# Revit family: METEOR_Atria II 6_REVIT_File (Standard)
name_source: partatom
category: Lighting Fixtures
revit_build: Autodesk Revit 2017 (Build: 20160225_1515(x64)
units: mm (PartAtom-declared; Revit-internal decimal feet)

## family parameters
Always vertical = Yes
Cut with Voids When Loaded = No
Host = Ceiling
Light Source = Yes
OmniClass Number = 23.80.70.11
OmniClass Title = Luminaries for Internal Lighting
Part Type = Normal
Room Calculation Point = No
Round Connector Dimension = Use Diameter
Shared = No

## types (48) — shared parameters
Color Filter = 16777215
Dimming Lamp Color Temperature Shift = <None>
Tilt Angle = 90.00°

## per-type parameters (varying)
| type | Photometric Web File |
| ASII6-60W-278-40 | ASII6-60-278-XXX-XXX-40-XXX.ies |
| ASII6-60W-278-60 | ASII6-60-278-XXX-XXX-60-XXX.ies |
| ASII6-60W-278-WD | ASII6-60-278-XXX-XXX-WD-XXX-DF.ies |
| ASII6-60W-308-40 | ASII6-60-308-XXX-XXX-40-XXX.ies |
| ASII6-60W-308-60 | ASII6-60-308-XXX-XXX-60-XXX.ies |
| ASII6-60W-308-WD | ASII6-60-308-XXX-XXX-WD-XXX-DF.ies |
| ASII6-60W-358-40 | ASII6-60-358-XXX-XXX-40-XXX.ies |
| ASII6-60W-358-60 | ASII6-60-358-XXX-XXX-60-XXX.ies |
| ASII6-60W-358-WD | ASII6-60-358-XXX-XXX-WD-XXX-DF.ies |
| ASII6-60W-408-40 | ASII6-60-408-XXX-XXX-40-XXX.ies |
| ASII6-40W-278-40 | ASII6-40-278-XXX-XXX-40-XXX.ies |
| ASII6-40W-278-60 | ASII6-40-278-XXX-XXX-60-XXX.ies |
| ASII6-40W-278-WD | ASII6-40-278-XXX-XXX-WD-XXX-DF.ies |
| ASII6-60W-408-60 | ASII6-60-408-XXX-XXX-60-XXX.ies |
| ASII6-60W-408-WD | ASII6-60-408-XXX-XXX-WD-XXX-DF.ies |
| ASII6-40W-308-40 | ASII6-40-308-XXX-XXX-40-XXX.ies |
| ASII6-40W-308-60 | ASII6-40-308-XXX-XXX-60-XXX.ies |
| ASII6-40W-308-WD | ASII6-40-308-XXX-XXX-WD-XXX-DF.ies |
| ASII6-40W-358-40 | ASII6-40-358-XXX-XXX-40-XXX.ies |
| ASII6-40W-358-60 | ASII6-40-358-XXX-XXX-60-XXX.ies |
| ASII6-40W-358-WD | ASII6-40-358-XXX-XXX-WD-XXX-DF.ies |
| ASII6-40W-408-40 | ASII6-40-408-XXX-XXX-40-XXX.ies |
| ASII6-40W-408-60 | ASII6-40-408-XXX-XXX-60-XXX.ies |
| ASII6-40W-408-WD | ASII6-40-408-XXX-XXX-WD-XXX-DF.ies |
| ASII6-80W-278-40 | ASII6-80-278-XXX-XXX-40-XXX.ies |
| ASII6-80W-278-60 | ASII6-80-278-XXX-XXX-60-XXX.ies |
| ASII6-80W-278-WD | ASII6-80-278-XXX-XXX-WD-XXX-DF.ies |
| ASII6-80W-308-40 | ASII6-80-308-XXX-XXX-40-XXX.ies |
| ASII6-80W-308-60 | ASII6-80-308-XXX-XXX-60-XXX.ies |
| ASII6-80W-308-WD | ASII6-80-308-XXX-XXX-60-XXX.ies |
| ASII6-80W-358-40 | ASII6-80-358-XXX-XXX-40-XXX.ies |
| ASII6-80W-358-60 | ASII6-80-358-XXX-XXX-60-XXX.ies |
| ASII6-80W-358-WD | ASII6-80-358-XXX-XXX-WD-XXX-DF.ies |
| ASII6-80W-408-40 | ASII6-80-408-XXX-XXX-40-XXX.ies |
| ASII6-80W-408-60 | ASII6-80-408-XXX-XXX-60-XXX.ies |
| ASII6-80W-408-WD | ASII6-80-408-XXX-XXX-WD-XXX-DF.ies |
| ASII6-100W-278-40 | ASII6-100-278-XXX-XXX-40-XXX.ies |
| ASII6-100W-278-60 | ASII6-100-278-XXX-XXX-60-XXX.ies |
| ASII6-100W-278-WD | ASII6-100-278-XXX-XXX-WD-XXX-DF.ies |
| ASII6-100W-308-40 | ASII6-100-308-XXX-XXX-40-XXX.ies |
| ASII6-100W-308-60 | ASII6-100-308-XXX-XXX-60-XXX.ies |
| ASII6-100W-308-WD | ASII6-100-308-XXX-XXX-WD-XXX-DF.ies |
| ASII6-100W-358-40 | ASII6-100-358-XXX-XXX-40-XXX.ies |
| ASII6-100W-358-60 | ASII6-100-358-XXX-XXX-60-XXX.ies |
| ASII6-100W-358-WD | ASII6-100-358-XXX-XXX-WD-XXX-DF.ies |
| ASII6-100W-408-40 | ASII6-100-408-XXX-XXX-40-XXX.ies |
| ASII6-100W-408-60 | ASII6-100-408-XXX-XXX-60-XXX.ies |
| ASII6-100W-408-WD | ASII6-100-408-XXX-XXX-WD-XXX-DF.ies |

note: column(s) folded — value = type name in every type: Lamp
